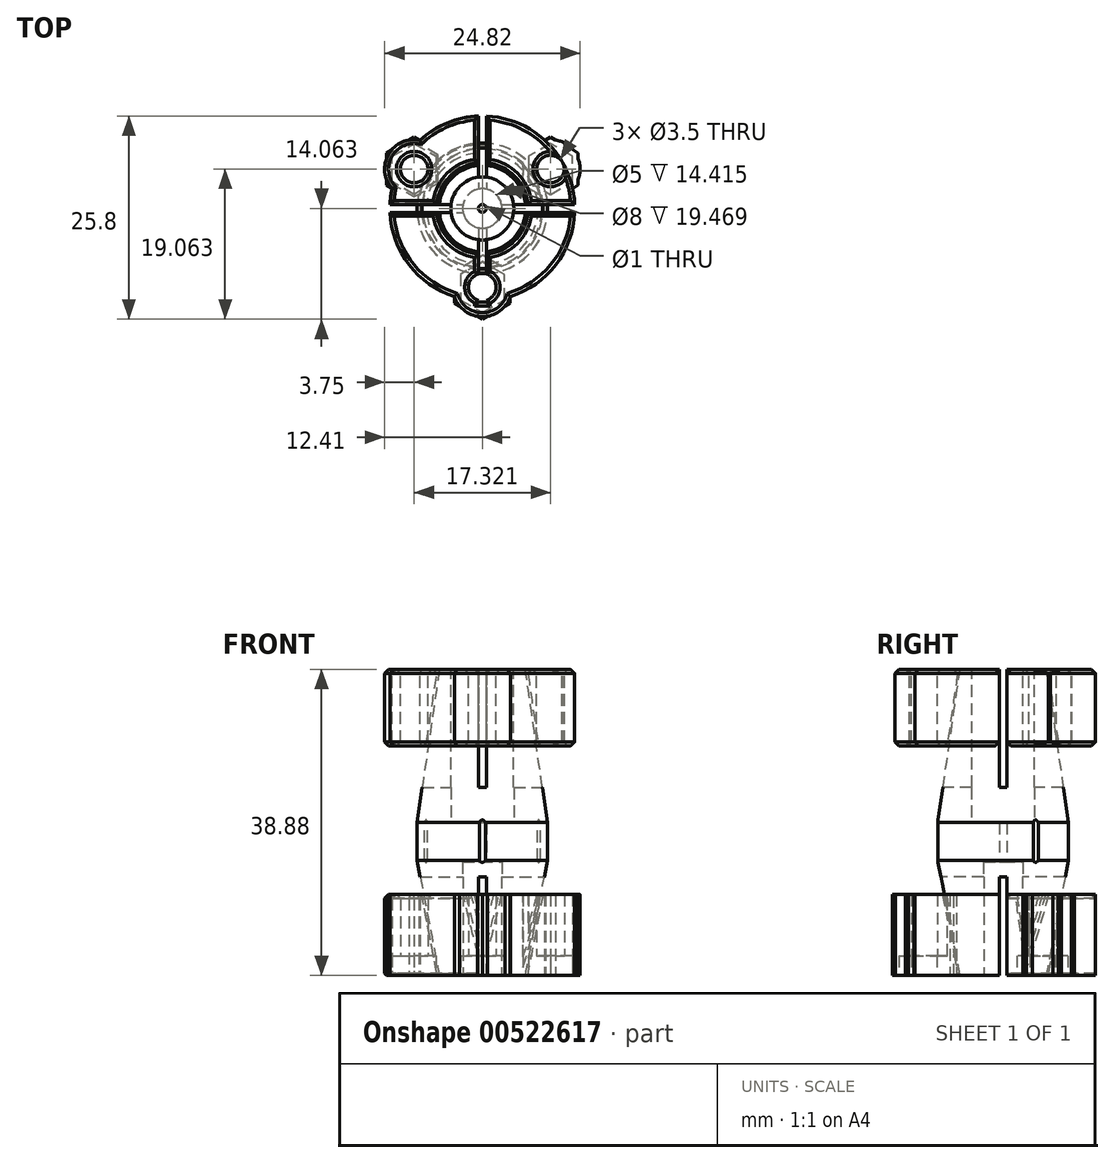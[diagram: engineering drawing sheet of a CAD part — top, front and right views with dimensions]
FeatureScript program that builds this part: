
annotation { "Feature Type Name" : "Feature", "Feature Type Description" : "" }
export const myFeature = defineFeature(function(context is Context, id is Id, definition is map)
    precondition{}
    {
        {
            var Q0;
            Q0=qCreatedBy(makeId("Right.planeOp"),FACE);
            var sketch = newSketch(context, id + "F0", { "sketchPlane" : qUnion([Q0])});
            skLineSegment(sketch, "E0", {"start": v(7.15, -27.2) * mm, "end": v(7.15, -12.78) * mm});
            skLineSegment(sketch, "E1", {"start": v(7.15, -12.78) * mm, "end": v(5.15, -12.78) * mm});
            skLineSegment(sketch, "E2", {"start": v(5.15, -12.78) * mm, "end": v(5.15, -7.78) * mm});
            skLineSegment(sketch, "E3", {"start": v(5.15, -7.78) * mm, "end": v(8.65, -7.78) * mm});
            skLineSegment(sketch, "E4", {"start": v(8.65, -7.78) * mm, "end": v(8.65, 11.68) * mm});
            skLineSegment(sketch, "E5", {"start": v(8.65, 11.68) * mm, "end": v(10.13, 11.68) * mm});
            skLineSegment(sketch, "E6", {"start": v(10.13, 11.68) * mm, "end": v(12.95, -7.78) * mm});
            skLineSegment(sketch, "E7", {"start": v(12.95, -7.78) * mm, "end": v(12.95, -12.57) * mm});
            skLineSegment(sketch, "E8", {"start": v(12.95, -12.57) * mm, "end": v(10.13, -27.2) * mm});
            skLineSegment(sketch, "E9", {"start": v(10.13, -27.2) * mm, "end": v(7.15, -27.2) * mm});
            skLineSegment(sketch, "E10", {"start": v(4.65, -27.22) * mm, "end": v(4.65, -0.97) * mm});
            skLineSegment(sketch, "E11", {"start": v(11.8, 1.95) * mm, "end": v(10.39, 11.68) * mm});
            skPoint(sketch, "E11.startSnap0", {"position": v(11.54, 1.95) * mm});
            skLineSegment(sketch, "E12", {"start": v(10.39, 11.68) * mm, "end": v(16.4, 11.68) * mm});
            skLineSegment(sketch, "E13", {"start": v(16.4, 11.68) * mm, "end": v(16.4, 1.95) * mm});
            skLineSegment(sketch, "E14", {"start": v(16.4, 1.95) * mm, "end": v(11.8, 1.95) * mm});
            skLineSegment(sketch, "E15", {"start": v(10.39, -27.2) * mm, "end": v(12.37, -16.92) * mm});
            skLineSegment(sketch, "E16", {"start": v(12.37, -16.92) * mm, "end": v(16.4, -16.92) * mm});
            skLineSegment(sketch, "E17", {"start": v(16.4, -16.92) * mm, "end": v(16.4, -27.2) * mm});
            skLineSegment(sketch, "E18", {"start": v(16.4, -27.2) * mm, "end": v(10.39, -27.2) * mm});
            skSolve(sketch);
        }
        {
            var Q0;
            Q0=makeQuery(id+"F0.imprint","IMPRINT",FACE,{"disambiguationData":[TD([[makeQuery(id+"F0.imprint","IMPRINT",EDGE,{"derivedFrom":sQuery(id+"F0.wireOp",EDGE,"E0")}),-1.0]])]});
            var Q1;
            Q1=sQuery(id+"F0.wireOp",EDGE,"E10");
            revolve(context, id + "F1", {"entities" : qUnion([Q0]), "axis" : qUnion([Q1]), "revolveType" : RevolveType.FULL});
        }
        {
            var Q0;
            Q0=makeQuery(id+"F0.imprint","IMPRINT",FACE,{"disambiguationData":[TD([[makeQuery(id+"F0.imprint","IMPRINT",EDGE,{"derivedFrom":sQuery(id+"F0.wireOp",EDGE,"E11")}),-1.0]])]});
            var Q1;
            Q1=makeQuery(id+"F0.imprint","IMPRINT",FACE,{"disambiguationData":[TD([[makeQuery(id+"F0.imprint","IMPRINT",EDGE,{"derivedFrom":sQuery(id+"F0.wireOp",EDGE,"E15")}),-1.0]])]});
            var Q2;
            Q2=sQuery(id+"F0.wireOp",EDGE,"E10");
            revolve(context, id + "F2", {"entities" : qUnion([Q0, Q1]), "axis" : qUnion([Q2]), "revolveType" : RevolveType.FULL});
        }
        {
            var Q0;
            Q0=makeQuery(id+"F2.opRevolve","SWEPT_FACE",FACE,{"disambiguationData":[OSD([sQuery(id+"F0.wireOp",EDGE,"E12")])]});
            var sketch = newSketch(context, id + "F3", { "sketchPlane" : qUnion([Q0])});
            skCircle(sketch, "E19", {"center": v(0, 4.65) * mm, "radius": 10 * mm});
            skCircle(sketch, "E20", {"center": v(0, -5.35) * mm, "radius": 1.75 * mm});
            skCircle(sketch, "E21", {"center": v(0, -5.35) * mm, "radius": 3.75 * mm});
            skCircle(sketch, "E22.1.0", {"center": v(8.66, 9.65) * mm, "radius": 1.75 * mm});
            skCircle(sketch, "E22.1.1", {"center": v(8.66, 9.65) * mm, "radius": 3.75 * mm});
            skCircle(sketch, "E22.2.0", {"center": v(-8.66, 9.65) * mm, "radius": 1.75 * mm});
            skCircle(sketch, "E22.2.1", {"center": v(-8.66, 9.65) * mm, "radius": 3.75 * mm});
            skSolve(sketch);
        }
        {
            var Q0;
            {var subQ0=sQuery(id+"F3.wireOp",EDGE,"E20");var subQ1=makeQuery(id+"F2.opRevolve","SWEPT_EDGE",EDGE,{"disambiguationData":[OSD([sQuery(id+"F0.wireOp",EDGE,"E12"),sQuery(id+"F0.wireOp",EDGE,"E13")])]});var subQ2=makeQuery(id+"F3.imprint","INTERSECT",VERTEX,{"disambiguationData":[OD(0.0)],"derivedFrom":[subQ1,subQ0]});Q0=makeQuery(id+"F3.imprint","IMPRINT",FACE,{"disambiguationData":[TD([[makeQuery(id+"F3.imprint","IMPRINT",EDGE,{"disambiguationData":[TD([[subQ2,-1.0]])],"derivedFrom":subQ0}),-1.0]])]});}
            var Q1;
            {var subQ0=sQuery(id+"F3.wireOp",EDGE,"E22.2.0");var subQ1=makeQuery(id+"F2.opRevolve","SWEPT_EDGE",EDGE,{"disambiguationData":[OSD([sQuery(id+"F0.wireOp",EDGE,"E12"),sQuery(id+"F0.wireOp",EDGE,"E13")])]});var subQ2=makeQuery(id+"F3.imprint","INTERSECT",VERTEX,{"disambiguationData":[OD(0.0)],"derivedFrom":[subQ1,subQ0]});Q1=makeQuery(id+"F3.imprint","IMPRINT",FACE,{"disambiguationData":[TD([[makeQuery(id+"F3.imprint","IMPRINT",EDGE,{"disambiguationData":[TD([[subQ2,-1.0]])],"derivedFrom":subQ0}),-1.0]])]});}
            var Q2;
            {var subQ0=sQuery(id+"F3.wireOp",EDGE,"E22.1.0");var subQ1=makeQuery(id+"F2.opRevolve","SWEPT_EDGE",EDGE,{"disambiguationData":[OSD([sQuery(id+"F0.wireOp",EDGE,"E12"),sQuery(id+"F0.wireOp",EDGE,"E13")])]});var subQ2=makeQuery(id+"F3.imprint","INTERSECT",VERTEX,{"disambiguationData":[OD(0.0)],"derivedFrom":[subQ1,subQ0]});Q2=makeQuery(id+"F3.imprint","IMPRINT",FACE,{"disambiguationData":[TD([[makeQuery(id+"F3.imprint","IMPRINT",EDGE,{"disambiguationData":[TD([[subQ2,-1.0]])],"derivedFrom":subQ0}),-1.0]])]});}
            var Q3;
            Q3=makeQuery(id+"F2.opRevolve","SWEPT_FACE",FACE,{"disambiguationData":[OSD([sQuery(id+"F0.wireOp",EDGE,"E14")])]});
            extrude(context, id + "F4", {"entities" : qUnion([Q0, Q1, Q2]), "operationType" : NewBodyOperationType.ADD, "endBound" : BoundingType.UP_TO_SURFACE, "oppositeDirection" : true, "endBoundEntityFace" : qUnion([Q3]), "depth" : 25 * mm});
        }
        {
            var Q0;
            {var subQ0=sQuery(id+"F3.wireOp",EDGE,"E20");var subQ1=sQuery(id+"F3.wireOp",EDGE,"E19");var subQ2=makeQuery(id+"F3.imprint","INTERSECT",VERTEX,{"disambiguationData":[OD(0.0)],"derivedFrom":[subQ1,subQ0]});Q0=makeQuery(id+"F3.imprint","IMPRINT",FACE,{"disambiguationData":[TD([[makeQuery(id+"F3.imprint","IMPRINT",EDGE,{"disambiguationData":[TD([[subQ2,-1.0]])],"derivedFrom":subQ1}),-1.0]])]});}
            var Q1;
            {var subQ0=sQuery(id+"F3.wireOp",EDGE,"E20");var subQ1=sQuery(id+"F3.wireOp",EDGE,"E19");var subQ2=makeQuery(id+"F3.imprint","INTERSECT",VERTEX,{"disambiguationData":[OD(0.0)],"derivedFrom":[subQ1,subQ0]});Q1=makeQuery(id+"F3.imprint","IMPRINT",FACE,{"disambiguationData":[TD([[makeQuery(id+"F3.imprint","IMPRINT",EDGE,{"disambiguationData":[TD([[subQ2,-1.0]])],"derivedFrom":subQ1}),1.0]])]});}
            var Q2;
            {var subQ0=sQuery(id+"F3.wireOp",EDGE,"E22.1.0");var subQ1=sQuery(id+"F3.wireOp",EDGE,"E19");var subQ2=makeQuery(id+"F3.imprint","INTERSECT",VERTEX,{"disambiguationData":[OD(0.0)],"derivedFrom":[subQ1,subQ0]});Q2=makeQuery(id+"F3.imprint","IMPRINT",FACE,{"disambiguationData":[TD([[makeQuery(id+"F3.imprint","IMPRINT",EDGE,{"disambiguationData":[TD([[subQ2,-1.0]])],"derivedFrom":subQ1}),1.0]])]});}
            var Q3;
            {var subQ0=sQuery(id+"F3.wireOp",EDGE,"E22.1.0");var subQ1=sQuery(id+"F3.wireOp",EDGE,"E19");var subQ2=makeQuery(id+"F3.imprint","INTERSECT",VERTEX,{"disambiguationData":[OD(0.0)],"derivedFrom":[subQ1,subQ0]});Q3=makeQuery(id+"F3.imprint","IMPRINT",FACE,{"disambiguationData":[TD([[makeQuery(id+"F3.imprint","IMPRINT",EDGE,{"disambiguationData":[TD([[subQ2,-1.0]])],"derivedFrom":subQ1}),-1.0]])]});}
            var Q4;
            {var subQ0=sQuery(id+"F3.wireOp",EDGE,"E22.2.0");var subQ1=sQuery(id+"F3.wireOp",EDGE,"E19");var subQ2=makeQuery(id+"F3.imprint","INTERSECT",VERTEX,{"disambiguationData":[OD(0.0)],"derivedFrom":[subQ1,subQ0]});Q4=makeQuery(id+"F3.imprint","IMPRINT",FACE,{"disambiguationData":[TD([[makeQuery(id+"F3.imprint","IMPRINT",EDGE,{"disambiguationData":[TD([[subQ2,-1.0]])],"derivedFrom":subQ1}),1.0]])]});}
            var Q5;
            {var subQ0=sQuery(id+"F3.wireOp",EDGE,"E22.2.0");var subQ1=sQuery(id+"F3.wireOp",EDGE,"E19");var subQ2=makeQuery(id+"F3.imprint","INTERSECT",VERTEX,{"disambiguationData":[OD(0.0)],"derivedFrom":[subQ1,subQ0]});Q5=makeQuery(id+"F3.imprint","IMPRINT",FACE,{"disambiguationData":[TD([[makeQuery(id+"F3.imprint","IMPRINT",EDGE,{"disambiguationData":[TD([[subQ2,-1.0]])],"derivedFrom":subQ1}),-1.0]])]});}
            extrude(context, id + "F5", {"entities" : qUnion([Q0, Q1, Q2, Q3, Q4, Q5]), "operationType" : NewBodyOperationType.REMOVE, "oppositeDirection" : true, "depth" : 25 * mm});
        }
        {
            var Q0;
            Q0=makeQuery(id+"F2.opRevolve","SWEPT_FACE",FACE,{"disambiguationData":[OSD([sQuery(id+"F0.wireOp",EDGE,"E18")])]});
            var sketch = newSketch(context, id + "F6", { "sketchPlane" : qUnion([Q0])});
            skArc(sketch, "E23.0.0", {"start": v(-3.55, 6.54) * mm, "mid": v(-10.17, 1.22) * mm, "end": v(-11.47, -7.17) * mm});
            skArc(sketch, "E23.0.1", {"start": v(-11.47, -7.17) * mm, "mid": v(-11.9, -11.53) * mm, "end": v(-7.92, -13.33) * mm});
            skArc(sketch, "E23.0.2", {"start": v(-7.92, -13.33) * mm, "mid": v(0, -16.4) * mm, "end": v(7.92, -13.33) * mm});
            skArc(sketch, "E23.0.3", {"start": v(7.92, -13.33) * mm, "mid": v(11.9, -11.53) * mm, "end": v(11.47, -7.17) * mm});
            skArc(sketch, "E23.0.4", {"start": v(11.47, -7.17) * mm, "mid": v(10.17, 1.22) * mm, "end": v(3.55, 6.54) * mm});
            skArc(sketch, "E23.0.5", {"start": v(3.55, 6.54) * mm, "mid": v(0, 9.1) * mm, "end": v(-3.55, 6.54) * mm});
            skCircle(sketch, "E24", {"center": v(8.66, -9.65) * mm, "radius": 1.75 * mm});
            skCircle(sketch, "E25", {"center": v(-8.66, -9.65) * mm, "radius": 1.75 * mm});
            skCircle(sketch, "E26", {"center": v(0, 5.35) * mm, "radius": 1.75 * mm});
            skSolve(sketch);
        }
        {
            var Q0;
            {var subQ0=sQuery(id+"F6.wireOp",EDGE,"E23.0.5");Q0=makeQuery(id+"F6.imprint","IMPRINT",FACE,{"disambiguationData":[TD([[makeQuery(id+"F6.imprint","IMPRINT",EDGE,{"derivedFrom":subQ0}),1.0]])]});}
            var Q1;
            {var subQ0=sQuery(id+"F6.wireOp",EDGE,"E23.0.3");Q1=makeQuery(id+"F6.imprint","IMPRINT",FACE,{"disambiguationData":[TD([[makeQuery(id+"F6.imprint","IMPRINT",EDGE,{"derivedFrom":subQ0}),1.0]])]});}
            var Q2;
            {var subQ0=sQuery(id+"F6.wireOp",EDGE,"E23.0.1");Q2=makeQuery(id+"F6.imprint","IMPRINT",FACE,{"disambiguationData":[TD([[makeQuery(id+"F6.imprint","IMPRINT",EDGE,{"derivedFrom":subQ0}),1.0]])]});}
            var Q3;
            Q3=makeQuery(id+"F2.opRevolve","SWEPT_FACE",FACE,{"disambiguationData":[OSD([sQuery(id+"F0.wireOp",EDGE,"E16")])]});
            extrude(context, id + "F7", {"entities" : qUnion([Q0, Q1, Q2]), "operationType" : NewBodyOperationType.ADD, "endBound" : BoundingType.UP_TO_SURFACE, "oppositeDirection" : true, "endBoundEntityFace" : qUnion([Q3]), "depth" : 25 * mm});
        }
        {
            var Q0;
            {var subQ0=sQuery(id+"F6.wireOp",EDGE,"E26");var subQ1=makeQuery(id+"F2.opRevolve","SWEPT_EDGE",EDGE,{"disambiguationData":[OSD([sQuery(id+"F0.wireOp",EDGE,"E17"),sQuery(id+"F0.wireOp",EDGE,"E18")])]});var subQ2=makeQuery(id+"F6.imprint","INTERSECT",VERTEX,{"disambiguationData":[OD(0.0)],"derivedFrom":[subQ1,subQ0]});Q0=makeQuery(id+"F6.imprint","IMPRINT",FACE,{"disambiguationData":[TD([[makeQuery(id+"F6.imprint","IMPRINT",EDGE,{"disambiguationData":[TD([[subQ2,-1.0]])],"derivedFrom":subQ0}),1.0]])]});}
            var Q1;
            {var subQ0=sQuery(id+"F6.wireOp",EDGE,"E25");var subQ1=makeQuery(id+"F2.opRevolve","SWEPT_EDGE",EDGE,{"disambiguationData":[OSD([sQuery(id+"F0.wireOp",EDGE,"E17"),sQuery(id+"F0.wireOp",EDGE,"E18")])]});var subQ2=makeQuery(id+"F6.imprint","INTERSECT",VERTEX,{"disambiguationData":[OD(0.0)],"derivedFrom":[subQ1,subQ0]});Q1=makeQuery(id+"F6.imprint","IMPRINT",FACE,{"disambiguationData":[TD([[makeQuery(id+"F6.imprint","IMPRINT",EDGE,{"disambiguationData":[TD([[subQ2,1.0]])],"derivedFrom":subQ0}),1.0]])]});}
            var Q2;
            {var subQ0=sQuery(id+"F6.wireOp",EDGE,"E24");var subQ1=makeQuery(id+"F2.opRevolve","SWEPT_EDGE",EDGE,{"disambiguationData":[OSD([sQuery(id+"F0.wireOp",EDGE,"E17"),sQuery(id+"F0.wireOp",EDGE,"E18")])]});var subQ2=makeQuery(id+"F6.imprint","INTERSECT",VERTEX,{"disambiguationData":[OD(0.0)],"derivedFrom":[subQ1,subQ0]});Q2=makeQuery(id+"F6.imprint","IMPRINT",FACE,{"disambiguationData":[TD([[makeQuery(id+"F6.imprint","IMPRINT",EDGE,{"disambiguationData":[TD([[subQ2,1.0]])],"derivedFrom":subQ0}),1.0]])]});}
            extrude(context, id + "F8", {"entities" : qUnion([Q0, Q1, Q2]), "operationType" : NewBodyOperationType.REMOVE, "oppositeDirection" : true, "depth" : 25 * mm});
        }
        {
            var Q0;
            Q0=makeQuery(id+"F1.opRevolve","SWEPT_FACE",FACE,{"disambiguationData":[OSD([sQuery(id+"F0.wireOp",EDGE,"E5")])]});
            var sketch = newSketch(context, id + "F9", { "sketchPlane" : qUnion([Q0])});
            skLineSegment(sketch, "E27.bottom", {"start": v(0.5, 16.55) * mm, "end": v(-0.5, 16.55) * mm});
            skLineSegment(sketch, "E27.top", {"start": v(0.5, -7.24) * mm, "end": v(-0.5, -7.24) * mm});
            skLineSegment(sketch, "E27.left", {"start": v(0.5, 16.55) * mm, "end": v(0.5, -7.24) * mm});
            skLineSegment(sketch, "E27.right", {"start": v(-0.5, 16.55) * mm, "end": v(-0.5, -7.24) * mm});
            skLineSegment(sketch, "E28.bottom", {"start": v(-15.2, 5.15) * mm, "end": v(15.2, 5.15) * mm});
            skLineSegment(sketch, "E28.top", {"start": v(-15.2, 4.15) * mm, "end": v(15.2, 4.15) * mm});
            skLineSegment(sketch, "E28.left", {"start": v(-15.2, 5.15) * mm, "end": v(-15.2, 4.15) * mm});
            skLineSegment(sketch, "E28.right", {"start": v(15.2, 5.15) * mm, "end": v(15.2, 4.15) * mm});
            skPoint(sketch, "E28.middle", {"position": v(0, 4.65) * mm});
            skSolve(sketch);
        }
        {
            var Q0;
            {var subQ0=sQuery(id+"F9.wireOp",EDGE,"E28.bottom");var subQ1=sQuery(id+"F9.wireOp",EDGE,"E27.left");var subQ2=makeQuery(id+"F9.imprint","INTERSECT",VERTEX,{"derivedFrom":[subQ1,subQ0]});Q0=makeQuery(id+"F9.imprint","IMPRINT",FACE,{"disambiguationData":[TD([[makeQuery(id+"F9.imprint","IMPRINT",EDGE,{"disambiguationData":[TD([[subQ2,-1.0]])],"derivedFrom":subQ1}),-1.0]])]});}
            var Q1;
            {var subQ0=sQuery(id+"F9.wireOp",EDGE,"E27.bottom");Q1=makeQuery(id+"F9.imprint","IMPRINT",FACE,{"disambiguationData":[TD([[makeQuery(id+"F9.imprint","IMPRINT",EDGE,{"derivedFrom":subQ0}),1.0]])]});}
            var Q2;
            {var subQ0=sQuery(id+"F9.wireOp",EDGE,"E27.top");Q2=makeQuery(id+"F9.imprint","IMPRINT",FACE,{"disambiguationData":[TD([[makeQuery(id+"F9.imprint","IMPRINT",EDGE,{"derivedFrom":subQ0}),-1.0]])]});}
            var Q3;
            {var subQ0=sQuery(id+"F9.wireOp",EDGE,"E28.bottom");var subQ1=sQuery(id+"F9.wireOp",EDGE,"E27.left");var subQ2=makeQuery(id+"F9.imprint","INTERSECT",VERTEX,{"derivedFrom":[subQ1,subQ0]});Q3=makeQuery(id+"F9.imprint","IMPRINT",FACE,{"disambiguationData":[TD([[makeQuery(id+"F9.imprint","IMPRINT",EDGE,{"disambiguationData":[TD([[subQ2,1.0]])],"derivedFrom":subQ0}),1.0]])]});}
            var Q4;
            {var subQ0=sQuery(id+"F9.wireOp",EDGE,"E28.top");var subQ1=sQuery(id+"F9.wireOp",EDGE,"E27.left");var subQ2=makeQuery(id+"F9.imprint","INTERSECT",VERTEX,{"derivedFrom":[subQ1,subQ0]});Q4=makeQuery(id+"F9.imprint","IMPRINT",FACE,{"disambiguationData":[TD([[makeQuery(id+"F9.imprint","IMPRINT",EDGE,{"disambiguationData":[TD([[subQ2,1.0]])],"derivedFrom":subQ0}),-1.0]])]});}
            var Q5;
            {var subQ0=sQuery(id+"F9.wireOp",EDGE,"E27.left");var subQ1=sQuery(id+"F0.wireOp",EDGE,"E5");var subQ2=makeQuery(id+"F1.opRevolve","SWEPT_EDGE",EDGE,{"disambiguationData":[OSD([subQ1,sQuery(id+"F0.wireOp",EDGE,"E6")])]});var subQ3=makeQuery(id+"F9.imprint","INTERSECT",VERTEX,{"disambiguationData":[OD(0.0)],"derivedFrom":[subQ2,subQ0]});Q5=makeQuery(id+"F9.imprint","IMPRINT",FACE,{"disambiguationData":[TD([[makeQuery(id+"F9.imprint","IMPRINT",EDGE,{"disambiguationData":[TD([[subQ3,-1.0]])],"derivedFrom":subQ0}),-1.0]])]});}
            var Q6;
            {var subQ0=sQuery(id+"F9.wireOp",EDGE,"E28.bottom");var subQ1=sQuery(id+"F9.wireOp",EDGE,"E27.left");var subQ2=makeQuery(id+"F9.imprint","INTERSECT",VERTEX,{"derivedFrom":[subQ1,subQ0]});Q6=makeQuery(id+"F9.imprint","IMPRINT",FACE,{"disambiguationData":[TD([[makeQuery(id+"F9.imprint","IMPRINT",EDGE,{"disambiguationData":[TD([[subQ2,-1.0]])],"derivedFrom":subQ1}),-1.0]])]});}
            var Q7;
            {var subQ0=sQuery(id+"F9.wireOp",EDGE,"E27.bottom");Q7=makeQuery(id+"F9.imprint","IMPRINT",FACE,{"disambiguationData":[TD([[makeQuery(id+"F9.imprint","IMPRINT",EDGE,{"derivedFrom":subQ0}),1.0]])]});}
            var Q8;
            {var subQ0=sQuery(id+"F9.wireOp",EDGE,"E27.top");Q8=makeQuery(id+"F9.imprint","IMPRINT",FACE,{"disambiguationData":[TD([[makeQuery(id+"F9.imprint","IMPRINT",EDGE,{"derivedFrom":subQ0}),-1.0]])]});}
            var Q9;
            {var subQ0=sQuery(id+"F9.wireOp",EDGE,"E28.bottom");var subQ1=sQuery(id+"F9.wireOp",EDGE,"E27.left");var subQ2=makeQuery(id+"F9.imprint","INTERSECT",VERTEX,{"derivedFrom":[subQ1,subQ0]});Q9=makeQuery(id+"F9.imprint","IMPRINT",FACE,{"disambiguationData":[TD([[makeQuery(id+"F9.imprint","IMPRINT",EDGE,{"disambiguationData":[TD([[subQ2,1.0]])],"derivedFrom":subQ0}),1.0]])]});}
            var Q10;
            {var subQ0=sQuery(id+"F9.wireOp",EDGE,"E28.top");var subQ1=sQuery(id+"F9.wireOp",EDGE,"E27.left");var subQ2=makeQuery(id+"F9.imprint","INTERSECT",VERTEX,{"derivedFrom":[subQ1,subQ0]});Q10=makeQuery(id+"F9.imprint","IMPRINT",FACE,{"disambiguationData":[TD([[makeQuery(id+"F9.imprint","IMPRINT",EDGE,{"disambiguationData":[TD([[subQ2,1.0]])],"derivedFrom":subQ0}),-1.0]])]});}
            var Q11;
            {var subQ0=sQuery(id+"F9.wireOp",EDGE,"E27.left");var subQ1=sQuery(id+"F0.wireOp",EDGE,"E5");var subQ2=makeQuery(id+"F1.opRevolve","SWEPT_EDGE",EDGE,{"disambiguationData":[OSD([subQ1,sQuery(id+"F0.wireOp",EDGE,"E6")])]});var subQ3=makeQuery(id+"F9.imprint","INTERSECT",VERTEX,{"disambiguationData":[OD(0.0)],"derivedFrom":[subQ2,subQ0]});Q11=makeQuery(id+"F9.imprint","IMPRINT",FACE,{"disambiguationData":[TD([[makeQuery(id+"F9.imprint","IMPRINT",EDGE,{"disambiguationData":[TD([[subQ3,-1.0]])],"derivedFrom":subQ0}),-1.0]])]});}
            var Q12;
            {var subQ0=sQuery(id+"F9.wireOp",EDGE,"E28.bottom");var subQ1=sQuery(id+"F9.wireOp",EDGE,"E27.left");var subQ2=makeQuery(id+"F9.imprint","INTERSECT",VERTEX,{"derivedFrom":[subQ1,subQ0]});Q12=makeQuery(id+"F9.imprint","IMPRINT",FACE,{"disambiguationData":[TD([[makeQuery(id+"F9.imprint","IMPRINT",EDGE,{"disambiguationData":[TD([[subQ2,-1.0]])],"derivedFrom":subQ1}),-1.0]])]});}
            var Q13;
            {var subQ0=sQuery(id+"F9.wireOp",EDGE,"E27.bottom");Q13=makeQuery(id+"F9.imprint","IMPRINT",FACE,{"disambiguationData":[TD([[makeQuery(id+"F9.imprint","IMPRINT",EDGE,{"derivedFrom":subQ0}),1.0]])]});}
            var Q14;
            {var subQ0=sQuery(id+"F9.wireOp",EDGE,"E27.top");Q14=makeQuery(id+"F9.imprint","IMPRINT",FACE,{"disambiguationData":[TD([[makeQuery(id+"F9.imprint","IMPRINT",EDGE,{"derivedFrom":subQ0}),-1.0]])]});}
            var Q15;
            {var subQ0=sQuery(id+"F9.wireOp",EDGE,"E28.bottom");var subQ1=sQuery(id+"F9.wireOp",EDGE,"E27.left");var subQ2=makeQuery(id+"F9.imprint","INTERSECT",VERTEX,{"derivedFrom":[subQ1,subQ0]});Q15=makeQuery(id+"F9.imprint","IMPRINT",FACE,{"disambiguationData":[TD([[makeQuery(id+"F9.imprint","IMPRINT",EDGE,{"disambiguationData":[TD([[subQ2,1.0]])],"derivedFrom":subQ0}),1.0]])]});}
            var Q16;
            {var subQ0=sQuery(id+"F9.wireOp",EDGE,"E28.top");var subQ1=sQuery(id+"F9.wireOp",EDGE,"E27.left");var subQ2=makeQuery(id+"F9.imprint","INTERSECT",VERTEX,{"derivedFrom":[subQ1,subQ0]});Q16=makeQuery(id+"F9.imprint","IMPRINT",FACE,{"disambiguationData":[TD([[makeQuery(id+"F9.imprint","IMPRINT",EDGE,{"disambiguationData":[TD([[subQ2,1.0]])],"derivedFrom":subQ0}),-1.0]])]});}
            var Q17;
            {var subQ0=sQuery(id+"F9.wireOp",EDGE,"E27.left");var subQ1=sQuery(id+"F0.wireOp",EDGE,"E5");var subQ2=makeQuery(id+"F1.opRevolve","SWEPT_EDGE",EDGE,{"disambiguationData":[OSD([subQ1,sQuery(id+"F0.wireOp",EDGE,"E6")])]});var subQ3=makeQuery(id+"F9.imprint","INTERSECT",VERTEX,{"disambiguationData":[OD(0.0)],"derivedFrom":[subQ2,subQ0]});Q17=makeQuery(id+"F9.imprint","IMPRINT",FACE,{"disambiguationData":[TD([[makeQuery(id+"F9.imprint","IMPRINT",EDGE,{"disambiguationData":[TD([[subQ3,-1.0]])],"derivedFrom":subQ0}),-1.0]])]});}
            var Q18;
            {var subQ0=sQuery(id+"F9.wireOp",EDGE,"E28.bottom");var subQ1=sQuery(id+"F9.wireOp",EDGE,"E27.left");var subQ2=makeQuery(id+"F9.imprint","INTERSECT",VERTEX,{"derivedFrom":[subQ1,subQ0]});Q18=makeQuery(id+"F9.imprint","IMPRINT",FACE,{"disambiguationData":[TD([[makeQuery(id+"F9.imprint","IMPRINT",EDGE,{"disambiguationData":[TD([[subQ2,-1.0]])],"derivedFrom":subQ1}),-1.0]])]});}
            var Q19;
            {var subQ0=sQuery(id+"F9.wireOp",EDGE,"E27.bottom");Q19=makeQuery(id+"F9.imprint","IMPRINT",FACE,{"disambiguationData":[TD([[makeQuery(id+"F9.imprint","IMPRINT",EDGE,{"derivedFrom":subQ0}),1.0]])]});}
            var Q20;
            {var subQ0=sQuery(id+"F9.wireOp",EDGE,"E27.top");Q20=makeQuery(id+"F9.imprint","IMPRINT",FACE,{"disambiguationData":[TD([[makeQuery(id+"F9.imprint","IMPRINT",EDGE,{"derivedFrom":subQ0}),-1.0]])]});}
            var Q21;
            {var subQ0=sQuery(id+"F9.wireOp",EDGE,"E28.bottom");var subQ1=sQuery(id+"F9.wireOp",EDGE,"E27.left");var subQ2=makeQuery(id+"F9.imprint","INTERSECT",VERTEX,{"derivedFrom":[subQ1,subQ0]});Q21=makeQuery(id+"F9.imprint","IMPRINT",FACE,{"disambiguationData":[TD([[makeQuery(id+"F9.imprint","IMPRINT",EDGE,{"disambiguationData":[TD([[subQ2,1.0]])],"derivedFrom":subQ0}),1.0]])]});}
            var Q22;
            {var subQ0=sQuery(id+"F9.wireOp",EDGE,"E28.top");var subQ1=sQuery(id+"F9.wireOp",EDGE,"E27.left");var subQ2=makeQuery(id+"F9.imprint","INTERSECT",VERTEX,{"derivedFrom":[subQ1,subQ0]});Q22=makeQuery(id+"F9.imprint","IMPRINT",FACE,{"disambiguationData":[TD([[makeQuery(id+"F9.imprint","IMPRINT",EDGE,{"disambiguationData":[TD([[subQ2,1.0]])],"derivedFrom":subQ0}),-1.0]])]});}
            var Q23;
            {var subQ0=sQuery(id+"F9.wireOp",EDGE,"E27.left");var subQ1=sQuery(id+"F0.wireOp",EDGE,"E5");var subQ2=makeQuery(id+"F1.opRevolve","SWEPT_EDGE",EDGE,{"disambiguationData":[OSD([subQ1,sQuery(id+"F0.wireOp",EDGE,"E6")])]});var subQ3=makeQuery(id+"F9.imprint","INTERSECT",VERTEX,{"disambiguationData":[OD(0.0)],"derivedFrom":[subQ2,subQ0]});Q23=makeQuery(id+"F9.imprint","IMPRINT",FACE,{"disambiguationData":[TD([[makeQuery(id+"F9.imprint","IMPRINT",EDGE,{"disambiguationData":[TD([[subQ3,-1.0]])],"derivedFrom":subQ0}),-1.0]])]});}
            var Q24;
            {var subQ0=sQuery(id+"F9.wireOp",EDGE,"E27.top");Q24=makeQuery(id+"F9.imprint","IMPRINT",FACE,{"disambiguationData":[TD([[makeQuery(id+"F9.imprint","IMPRINT",EDGE,{"derivedFrom":subQ0}),-1.0]])]});}
            var Q25;
            {var subQ0=sQuery(id+"F9.wireOp",EDGE,"E28.top");var subQ1=sQuery(id+"F9.wireOp",EDGE,"E27.left");var subQ2=makeQuery(id+"F9.imprint","INTERSECT",VERTEX,{"derivedFrom":[subQ1,subQ0]});Q25=makeQuery(id+"F9.imprint","IMPRINT",FACE,{"disambiguationData":[TD([[makeQuery(id+"F9.imprint","IMPRINT",EDGE,{"disambiguationData":[TD([[subQ2,-1.0]])],"derivedFrom":subQ1}),1.0]])]});}
            var Q26;
            {var subQ0=sQuery(id+"F9.wireOp",EDGE,"E28.top");var subQ1=sQuery(id+"F9.wireOp",EDGE,"E27.right");var subQ2=makeQuery(id+"F9.imprint","INTERSECT",VERTEX,{"derivedFrom":[subQ1,subQ0]});Q26=makeQuery(id+"F9.imprint","IMPRINT",FACE,{"disambiguationData":[TD([[makeQuery(id+"F9.imprint","IMPRINT",EDGE,{"disambiguationData":[TD([[subQ2,-1.0]])],"derivedFrom":subQ1}),-1.0]])]});}
            var Q27;
            {var subQ0=sQuery(id+"F9.wireOp",EDGE,"E28.top");var subQ1=sQuery(id+"F9.wireOp",EDGE,"E27.left");var subQ2=makeQuery(id+"F9.imprint","INTERSECT",VERTEX,{"derivedFrom":[subQ1,subQ0]});Q27=makeQuery(id+"F9.imprint","IMPRINT",FACE,{"disambiguationData":[TD([[makeQuery(id+"F9.imprint","IMPRINT",EDGE,{"disambiguationData":[TD([[subQ2,-1.0]])],"derivedFrom":subQ1}),1.0]])]});}
            var Q28;
            {var subQ0=sQuery(id+"F9.wireOp",EDGE,"E28.top");var subQ1=sQuery(id+"F9.wireOp",EDGE,"E27.right");var subQ2=makeQuery(id+"F9.imprint","INTERSECT",VERTEX,{"derivedFrom":[subQ1,subQ0]});Q28=makeQuery(id+"F9.imprint","IMPRINT",FACE,{"disambiguationData":[TD([[makeQuery(id+"F9.imprint","IMPRINT",EDGE,{"disambiguationData":[TD([[subQ2,-1.0]])],"derivedFrom":subQ1}),-1.0]])]});}
            var Q29;
            {var subQ0=sQuery(id+"F9.wireOp",EDGE,"E28.bottom");var subQ1=sQuery(id+"F9.wireOp",EDGE,"E27.left");var subQ2=makeQuery(id+"F9.imprint","INTERSECT",VERTEX,{"derivedFrom":[subQ1,subQ0]});Q29=makeQuery(id+"F9.imprint","IMPRINT",FACE,{"disambiguationData":[TD([[makeQuery(id+"F9.imprint","IMPRINT",EDGE,{"disambiguationData":[TD([[subQ2,-1.0]])],"derivedFrom":subQ1}),-1.0]])]});}
            var Q30;
            {var subQ0=sQuery(id+"F9.wireOp",EDGE,"E27.bottom");Q30=makeQuery(id+"F9.imprint","IMPRINT",FACE,{"disambiguationData":[TD([[makeQuery(id+"F9.imprint","IMPRINT",EDGE,{"derivedFrom":subQ0}),1.0]])]});}
            var Q31;
            {var subQ0=sQuery(id+"F9.wireOp",EDGE,"E27.top");Q31=makeQuery(id+"F9.imprint","IMPRINT",FACE,{"disambiguationData":[TD([[makeQuery(id+"F9.imprint","IMPRINT",EDGE,{"derivedFrom":subQ0}),-1.0]])]});}
            var Q32;
            {var subQ0=sQuery(id+"F9.wireOp",EDGE,"E28.bottom");var subQ1=sQuery(id+"F9.wireOp",EDGE,"E27.left");var subQ2=makeQuery(id+"F9.imprint","INTERSECT",VERTEX,{"derivedFrom":[subQ1,subQ0]});Q32=makeQuery(id+"F9.imprint","IMPRINT",FACE,{"disambiguationData":[TD([[makeQuery(id+"F9.imprint","IMPRINT",EDGE,{"disambiguationData":[TD([[subQ2,1.0]])],"derivedFrom":subQ0}),1.0]])]});}
            var Q33;
            {var subQ0=sQuery(id+"F9.wireOp",EDGE,"E28.top");var subQ1=sQuery(id+"F9.wireOp",EDGE,"E27.left");var subQ2=makeQuery(id+"F9.imprint","INTERSECT",VERTEX,{"derivedFrom":[subQ1,subQ0]});Q33=makeQuery(id+"F9.imprint","IMPRINT",FACE,{"disambiguationData":[TD([[makeQuery(id+"F9.imprint","IMPRINT",EDGE,{"disambiguationData":[TD([[subQ2,1.0]])],"derivedFrom":subQ0}),-1.0]])]});}
            var Q34;
            {var subQ0=sQuery(id+"F9.wireOp",EDGE,"E27.left");var subQ1=sQuery(id+"F0.wireOp",EDGE,"E5");var subQ2=makeQuery(id+"F1.opRevolve","SWEPT_EDGE",EDGE,{"disambiguationData":[OSD([subQ1,sQuery(id+"F0.wireOp",EDGE,"E6")])]});var subQ3=makeQuery(id+"F9.imprint","INTERSECT",VERTEX,{"disambiguationData":[OD(0.0)],"derivedFrom":[subQ2,subQ0]});Q34=makeQuery(id+"F9.imprint","IMPRINT",FACE,{"disambiguationData":[TD([[makeQuery(id+"F9.imprint","IMPRINT",EDGE,{"disambiguationData":[TD([[subQ3,-1.0]])],"derivedFrom":subQ0}),-1.0]])]});}
            var Q35;
            {var subQ0=sQuery(id+"F9.wireOp",EDGE,"E27.left");var subQ1=sQuery(id+"F0.wireOp",EDGE,"E5");var subQ2=makeQuery(id+"F1.opRevolve","SWEPT_EDGE",EDGE,{"disambiguationData":[OSD([subQ1,sQuery(id+"F0.wireOp",EDGE,"E6")])]});var subQ3=makeQuery(id+"F9.imprint","INTERSECT",VERTEX,{"disambiguationData":[OD(1.0)],"derivedFrom":[subQ2,subQ0]});Q35=makeQuery(id+"F9.imprint","IMPRINT",FACE,{"disambiguationData":[TD([[makeQuery(id+"F9.imprint","IMPRINT",EDGE,{"disambiguationData":[TD([[subQ3,1.0]])],"derivedFrom":subQ0}),-1.0]])]});}
            var Q36;
            {var subQ0=sQuery(id+"F9.wireOp",EDGE,"E28.bottom");var subQ1=sQuery(id+"F9.wireOp",EDGE,"E27.left");var subQ2=makeQuery(id+"F9.imprint","INTERSECT",VERTEX,{"derivedFrom":[subQ1,subQ0]});Q36=makeQuery(id+"F9.imprint","IMPRINT",FACE,{"disambiguationData":[TD([[makeQuery(id+"F9.imprint","IMPRINT",EDGE,{"disambiguationData":[TD([[subQ2,-1.0]])],"derivedFrom":subQ1}),-1.0]])]});}
            var Q37;
            {var subQ0=sQuery(id+"F9.wireOp",EDGE,"E27.bottom");Q37=makeQuery(id+"F9.imprint","IMPRINT",FACE,{"disambiguationData":[TD([[makeQuery(id+"F9.imprint","IMPRINT",EDGE,{"derivedFrom":subQ0}),1.0]])]});}
            var Q38;
            {var subQ0=sQuery(id+"F9.wireOp",EDGE,"E27.top");Q38=makeQuery(id+"F9.imprint","IMPRINT",FACE,{"disambiguationData":[TD([[makeQuery(id+"F9.imprint","IMPRINT",EDGE,{"derivedFrom":subQ0}),-1.0]])]});}
            var Q39;
            {var subQ0=sQuery(id+"F9.wireOp",EDGE,"E28.bottom");var subQ1=sQuery(id+"F9.wireOp",EDGE,"E27.left");var subQ2=makeQuery(id+"F9.imprint","INTERSECT",VERTEX,{"derivedFrom":[subQ1,subQ0]});Q39=makeQuery(id+"F9.imprint","IMPRINT",FACE,{"disambiguationData":[TD([[makeQuery(id+"F9.imprint","IMPRINT",EDGE,{"disambiguationData":[TD([[subQ2,1.0]])],"derivedFrom":subQ0}),1.0]])]});}
            var Q40;
            {var subQ0=sQuery(id+"F9.wireOp",EDGE,"E28.top");var subQ1=sQuery(id+"F9.wireOp",EDGE,"E27.left");var subQ2=makeQuery(id+"F9.imprint","INTERSECT",VERTEX,{"derivedFrom":[subQ1,subQ0]});Q40=makeQuery(id+"F9.imprint","IMPRINT",FACE,{"disambiguationData":[TD([[makeQuery(id+"F9.imprint","IMPRINT",EDGE,{"disambiguationData":[TD([[subQ2,1.0]])],"derivedFrom":subQ0}),-1.0]])]});}
            var Q41;
            {var subQ0=sQuery(id+"F9.wireOp",EDGE,"E27.left");var subQ1=sQuery(id+"F0.wireOp",EDGE,"E5");var subQ2=makeQuery(id+"F1.opRevolve","SWEPT_EDGE",EDGE,{"disambiguationData":[OSD([subQ1,sQuery(id+"F0.wireOp",EDGE,"E6")])]});var subQ3=makeQuery(id+"F9.imprint","INTERSECT",VERTEX,{"disambiguationData":[OD(0.0)],"derivedFrom":[subQ2,subQ0]});Q41=makeQuery(id+"F9.imprint","IMPRINT",FACE,{"disambiguationData":[TD([[makeQuery(id+"F9.imprint","IMPRINT",EDGE,{"disambiguationData":[TD([[subQ3,-1.0]])],"derivedFrom":subQ0}),-1.0]])]});}
            var Q42;
            {var subQ0=sQuery(id+"F9.wireOp",EDGE,"E27.left");var subQ1=sQuery(id+"F0.wireOp",EDGE,"E5");var subQ2=makeQuery(id+"F1.opRevolve","SWEPT_EDGE",EDGE,{"disambiguationData":[OSD([subQ1,sQuery(id+"F0.wireOp",EDGE,"E6")])]});var subQ3=makeQuery(id+"F9.imprint","INTERSECT",VERTEX,{"disambiguationData":[OD(1.0)],"derivedFrom":[subQ2,subQ0]});Q42=makeQuery(id+"F9.imprint","IMPRINT",FACE,{"disambiguationData":[TD([[makeQuery(id+"F9.imprint","IMPRINT",EDGE,{"disambiguationData":[TD([[subQ3,1.0]])],"derivedFrom":subQ0}),-1.0]])]});}
            var Q43;
            {var subQ0=sQuery(id+"F9.wireOp",EDGE,"E28.bottom");var subQ1=sQuery(id+"F9.wireOp",EDGE,"E27.left");var subQ2=makeQuery(id+"F9.imprint","INTERSECT",VERTEX,{"derivedFrom":[subQ1,subQ0]});Q43=makeQuery(id+"F9.imprint","IMPRINT",FACE,{"disambiguationData":[TD([[makeQuery(id+"F9.imprint","IMPRINT",EDGE,{"disambiguationData":[TD([[subQ2,-1.0]])],"derivedFrom":subQ1}),-1.0]])]});}
            var Q44;
            {var subQ0=sQuery(id+"F9.wireOp",EDGE,"E27.bottom");Q44=makeQuery(id+"F9.imprint","IMPRINT",FACE,{"disambiguationData":[TD([[makeQuery(id+"F9.imprint","IMPRINT",EDGE,{"derivedFrom":subQ0}),1.0]])]});}
            var Q45;
            {var subQ0=sQuery(id+"F9.wireOp",EDGE,"E27.top");Q45=makeQuery(id+"F9.imprint","IMPRINT",FACE,{"disambiguationData":[TD([[makeQuery(id+"F9.imprint","IMPRINT",EDGE,{"derivedFrom":subQ0}),-1.0]])]});}
            var Q46;
            {var subQ0=sQuery(id+"F9.wireOp",EDGE,"E28.bottom");var subQ1=sQuery(id+"F9.wireOp",EDGE,"E27.left");var subQ2=makeQuery(id+"F9.imprint","INTERSECT",VERTEX,{"derivedFrom":[subQ1,subQ0]});Q46=makeQuery(id+"F9.imprint","IMPRINT",FACE,{"disambiguationData":[TD([[makeQuery(id+"F9.imprint","IMPRINT",EDGE,{"disambiguationData":[TD([[subQ2,1.0]])],"derivedFrom":subQ0}),1.0]])]});}
            var Q47;
            {var subQ0=sQuery(id+"F9.wireOp",EDGE,"E28.top");var subQ1=sQuery(id+"F9.wireOp",EDGE,"E27.left");var subQ2=makeQuery(id+"F9.imprint","INTERSECT",VERTEX,{"derivedFrom":[subQ1,subQ0]});Q47=makeQuery(id+"F9.imprint","IMPRINT",FACE,{"disambiguationData":[TD([[makeQuery(id+"F9.imprint","IMPRINT",EDGE,{"disambiguationData":[TD([[subQ2,1.0]])],"derivedFrom":subQ0}),-1.0]])]});}
            var Q48;
            {var subQ0=sQuery(id+"F9.wireOp",EDGE,"E27.left");var subQ1=sQuery(id+"F0.wireOp",EDGE,"E5");var subQ2=makeQuery(id+"F1.opRevolve","SWEPT_EDGE",EDGE,{"disambiguationData":[OSD([subQ1,sQuery(id+"F0.wireOp",EDGE,"E6")])]});var subQ3=makeQuery(id+"F9.imprint","INTERSECT",VERTEX,{"disambiguationData":[OD(0.0)],"derivedFrom":[subQ2,subQ0]});Q48=makeQuery(id+"F9.imprint","IMPRINT",FACE,{"disambiguationData":[TD([[makeQuery(id+"F9.imprint","IMPRINT",EDGE,{"disambiguationData":[TD([[subQ3,-1.0]])],"derivedFrom":subQ0}),-1.0]])]});}
            var Q49;
            {var subQ0=sQuery(id+"F9.wireOp",EDGE,"E27.left");var subQ1=sQuery(id+"F0.wireOp",EDGE,"E5");var subQ2=makeQuery(id+"F1.opRevolve","SWEPT_EDGE",EDGE,{"disambiguationData":[OSD([subQ1,sQuery(id+"F0.wireOp",EDGE,"E6")])]});var subQ3=makeQuery(id+"F9.imprint","INTERSECT",VERTEX,{"disambiguationData":[OD(1.0)],"derivedFrom":[subQ2,subQ0]});Q49=makeQuery(id+"F9.imprint","IMPRINT",FACE,{"disambiguationData":[TD([[makeQuery(id+"F9.imprint","IMPRINT",EDGE,{"disambiguationData":[TD([[subQ3,1.0]])],"derivedFrom":subQ0}),-1.0]])]});}
            var Q50;
            {var subQ0=sQuery(id+"F9.wireOp",EDGE,"E28.bottom");var subQ1=sQuery(id+"F9.wireOp",EDGE,"E27.left");var subQ2=makeQuery(id+"F9.imprint","INTERSECT",VERTEX,{"derivedFrom":[subQ1,subQ0]});Q50=makeQuery(id+"F9.imprint","IMPRINT",FACE,{"disambiguationData":[TD([[makeQuery(id+"F9.imprint","IMPRINT",EDGE,{"disambiguationData":[TD([[subQ2,1.0]])],"derivedFrom":subQ1}),1.0]])]});}
            var Q51;
            {var subQ0=sQuery(id+"F9.wireOp",EDGE,"E28.bottom");var subQ1=sQuery(id+"F9.wireOp",EDGE,"E27.right");var subQ2=makeQuery(id+"F9.imprint","INTERSECT",VERTEX,{"derivedFrom":[subQ1,subQ0]});Q51=makeQuery(id+"F9.imprint","IMPRINT",FACE,{"disambiguationData":[TD([[makeQuery(id+"F9.imprint","IMPRINT",EDGE,{"disambiguationData":[TD([[subQ2,1.0]])],"derivedFrom":subQ1}),-1.0]])]});}
            var Q52;
            {var subQ0=sQuery(id+"F9.wireOp",EDGE,"E28.bottom");var subQ1=sQuery(id+"F9.wireOp",EDGE,"E27.left");var subQ2=makeQuery(id+"F9.imprint","INTERSECT",VERTEX,{"derivedFrom":[subQ1,subQ0]});Q52=makeQuery(id+"F9.imprint","IMPRINT",FACE,{"disambiguationData":[TD([[makeQuery(id+"F9.imprint","IMPRINT",EDGE,{"disambiguationData":[TD([[subQ2,1.0]])],"derivedFrom":subQ1}),1.0]])]});}
            var Q53;
            {var subQ0=sQuery(id+"F9.wireOp",EDGE,"E28.bottom");var subQ1=sQuery(id+"F9.wireOp",EDGE,"E27.right");var subQ2=makeQuery(id+"F9.imprint","INTERSECT",VERTEX,{"derivedFrom":[subQ1,subQ0]});Q53=makeQuery(id+"F9.imprint","IMPRINT",FACE,{"disambiguationData":[TD([[makeQuery(id+"F9.imprint","IMPRINT",EDGE,{"disambiguationData":[TD([[subQ2,1.0]])],"derivedFrom":subQ1}),-1.0]])]});}
            var Q54;
            {var subQ0=sQuery(id+"F9.wireOp",EDGE,"E27.bottom");Q54=makeQuery(id+"F9.imprint","IMPRINT",FACE,{"disambiguationData":[TD([[makeQuery(id+"F9.imprint","IMPRINT",EDGE,{"derivedFrom":subQ0}),1.0]])]});}
            var Q55;
            {var subQ0=sQuery(id+"F9.wireOp",EDGE,"E28.bottom");var subQ1=sQuery(id+"F9.wireOp",EDGE,"E27.left");var subQ2=makeQuery(id+"F9.imprint","INTERSECT",VERTEX,{"derivedFrom":[subQ1,subQ0]});Q55=makeQuery(id+"F9.imprint","IMPRINT",FACE,{"disambiguationData":[TD([[makeQuery(id+"F9.imprint","IMPRINT",EDGE,{"disambiguationData":[TD([[subQ2,1.0]])],"derivedFrom":subQ1}),1.0]])]});}
            var Q56;
            {var subQ0=sQuery(id+"F9.wireOp",EDGE,"E28.top");var subQ1=sQuery(id+"F9.wireOp",EDGE,"E27.left");var subQ2=makeQuery(id+"F9.imprint","INTERSECT",VERTEX,{"derivedFrom":[subQ1,subQ0]});Q56=makeQuery(id+"F9.imprint","IMPRINT",FACE,{"disambiguationData":[TD([[makeQuery(id+"F9.imprint","IMPRINT",EDGE,{"disambiguationData":[TD([[subQ2,-1.0]])],"derivedFrom":subQ1}),1.0]])]});}
            var Q57;
            {var subQ0=sQuery(id+"F9.wireOp",EDGE,"E28.bottom");var subQ1=sQuery(id+"F9.wireOp",EDGE,"E27.left");var subQ2=makeQuery(id+"F9.imprint","INTERSECT",VERTEX,{"derivedFrom":[subQ1,subQ0]});Q57=makeQuery(id+"F9.imprint","IMPRINT",FACE,{"disambiguationData":[TD([[makeQuery(id+"F9.imprint","IMPRINT",EDGE,{"disambiguationData":[TD([[subQ2,1.0]])],"derivedFrom":subQ1}),1.0]])]});}
            var Q58;
            {var subQ0=sQuery(id+"F9.wireOp",EDGE,"E28.top");var subQ1=sQuery(id+"F9.wireOp",EDGE,"E27.left");var subQ2=makeQuery(id+"F9.imprint","INTERSECT",VERTEX,{"derivedFrom":[subQ1,subQ0]});Q58=makeQuery(id+"F9.imprint","IMPRINT",FACE,{"disambiguationData":[TD([[makeQuery(id+"F9.imprint","IMPRINT",EDGE,{"disambiguationData":[TD([[subQ2,-1.0]])],"derivedFrom":subQ1}),1.0]])]});}
            var Q59;
            {var subQ0=sQuery(id+"F9.wireOp",EDGE,"E28.right");Q59=makeQuery(id+"F9.imprint","IMPRINT",FACE,{"disambiguationData":[TD([[makeQuery(id+"F9.imprint","IMPRINT",EDGE,{"derivedFrom":subQ0}),-1.0]])]});}
            var Q60;
            {var subQ0=sQuery(id+"F9.wireOp",EDGE,"E28.bottom");var subQ1=sQuery(id+"F9.wireOp",EDGE,"E27.right");var subQ2=makeQuery(id+"F9.imprint","INTERSECT",VERTEX,{"derivedFrom":[subQ1,subQ0]});Q60=makeQuery(id+"F9.imprint","IMPRINT",FACE,{"disambiguationData":[TD([[makeQuery(id+"F9.imprint","IMPRINT",EDGE,{"disambiguationData":[TD([[subQ2,1.0]])],"derivedFrom":subQ1}),-1.0]])]});}
            var Q61;
            {var subQ0=sQuery(id+"F9.wireOp",EDGE,"E28.top");var subQ1=sQuery(id+"F9.wireOp",EDGE,"E27.right");var subQ2=makeQuery(id+"F9.imprint","INTERSECT",VERTEX,{"derivedFrom":[subQ1,subQ0]});Q61=makeQuery(id+"F9.imprint","IMPRINT",FACE,{"disambiguationData":[TD([[makeQuery(id+"F9.imprint","IMPRINT",EDGE,{"disambiguationData":[TD([[subQ2,-1.0]])],"derivedFrom":subQ1}),-1.0]])]});}
            var Q62;
            {var subQ0=sQuery(id+"F9.wireOp",EDGE,"E28.bottom");var subQ1=sQuery(id+"F9.wireOp",EDGE,"E27.right");var subQ2=makeQuery(id+"F9.imprint","INTERSECT",VERTEX,{"derivedFrom":[subQ1,subQ0]});Q62=makeQuery(id+"F9.imprint","IMPRINT",FACE,{"disambiguationData":[TD([[makeQuery(id+"F9.imprint","IMPRINT",EDGE,{"disambiguationData":[TD([[subQ2,1.0]])],"derivedFrom":subQ1}),-1.0]])]});}
            var Q63;
            {var subQ0=sQuery(id+"F9.wireOp",EDGE,"E28.top");var subQ1=sQuery(id+"F9.wireOp",EDGE,"E27.right");var subQ2=makeQuery(id+"F9.imprint","INTERSECT",VERTEX,{"derivedFrom":[subQ1,subQ0]});Q63=makeQuery(id+"F9.imprint","IMPRINT",FACE,{"disambiguationData":[TD([[makeQuery(id+"F9.imprint","IMPRINT",EDGE,{"disambiguationData":[TD([[subQ2,-1.0]])],"derivedFrom":subQ1}),-1.0]])]});}
            var Q64;
            {var subQ0=sQuery(id+"F9.wireOp",EDGE,"E28.left");Q64=makeQuery(id+"F9.imprint","IMPRINT",FACE,{"disambiguationData":[TD([[makeQuery(id+"F9.imprint","IMPRINT",EDGE,{"derivedFrom":subQ0}),1.0]])]});}
            var Q65;
            {var subQ0=sQuery(id+"F9.wireOp",EDGE,"E28.bottom");var subQ1=sQuery(id+"F0.wireOp",EDGE,"E5");var subQ2=makeQuery(id+"F1.opRevolve","SWEPT_EDGE",EDGE,{"disambiguationData":[OSD([subQ1,sQuery(id+"F0.wireOp",EDGE,"E6")])]});var subQ3=makeQuery(id+"F9.imprint","INTERSECT",VERTEX,{"disambiguationData":[OD(0.0)],"derivedFrom":[subQ2,subQ0]});Q65=makeQuery(id+"F9.imprint","IMPRINT",FACE,{"disambiguationData":[TD([[makeQuery(id+"F9.imprint","IMPRINT",EDGE,{"disambiguationData":[TD([[subQ3,-1.0]])],"derivedFrom":subQ0}),-1.0]])]});}
            var Q66;
            {var subQ0=sQuery(id+"F9.wireOp",EDGE,"E28.bottom");var subQ1=sQuery(id+"F0.wireOp",EDGE,"E5");var subQ2=makeQuery(id+"F1.opRevolve","SWEPT_EDGE",EDGE,{"disambiguationData":[OSD([subQ1,sQuery(id+"F0.wireOp",EDGE,"E6")])]});var subQ3=makeQuery(id+"F9.imprint","INTERSECT",VERTEX,{"disambiguationData":[OD(1.0)],"derivedFrom":[subQ2,subQ0]});Q66=makeQuery(id+"F9.imprint","IMPRINT",FACE,{"disambiguationData":[TD([[makeQuery(id+"F9.imprint","IMPRINT",EDGE,{"disambiguationData":[TD([[subQ3,1.0]])],"derivedFrom":subQ0}),-1.0]])]});}
            extrude(context, id + "F10", {"entities" : qUnion([Q0, Q1, Q2, Q3, Q4, Q5, Q6, Q7, Q8, Q9, Q10, Q11, Q12, Q13, Q14, Q15, Q16, Q17, Q18, Q19, Q20, Q21, Q22, Q23, Q24, Q25, Q26, Q27, Q28, Q29, Q30, Q31, Q32, Q33, Q34, Q35, Q36, Q37, Q38, Q39, Q40, Q41, Q42, Q43, Q44, Q45, Q46, Q47, Q48, Q49, Q50, Q51, Q52, Q53, Q54, Q55, Q56, Q57, Q58, Q59, Q60, Q61, Q62, Q63, Q64, Q65, Q66]), "operationType" : NewBodyOperationType.REMOVE, "oppositeDirection" : true, "depth" : 15 * mm});
        }
        {
            var Q0;
            {var subQ0=sQuery(id+"F9.wireOp",EDGE,"E28.bottom");var subQ1=sQuery(id+"F9.wireOp",EDGE,"E27.left");var subQ2=makeQuery(id+"F9.imprint","INTERSECT",VERTEX,{"derivedFrom":[subQ1,subQ0]});Q0=makeQuery(id+"F9.imprint","IMPRINT",FACE,{"disambiguationData":[TD([[makeQuery(id+"F9.imprint","IMPRINT",EDGE,{"disambiguationData":[TD([[subQ2,-1.0]])],"derivedFrom":subQ1}),1.0]])]});}
            var Q1;
            {var subQ0=sQuery(id+"F9.wireOp",EDGE,"E28.bottom");var subQ1=sQuery(id+"F0.wireOp",EDGE,"E5");var subQ2=makeQuery(id+"F1.opRevolve","SWEPT_EDGE",EDGE,{"disambiguationData":[OSD([subQ1,sQuery(id+"F0.wireOp",EDGE,"E6")])]});var subQ3=makeQuery(id+"F9.imprint","INTERSECT",VERTEX,{"disambiguationData":[OD(1.0)],"derivedFrom":[subQ2,subQ0]});Q1=makeQuery(id+"F9.imprint","IMPRINT",FACE,{"disambiguationData":[TD([[makeQuery(id+"F9.imprint","IMPRINT",EDGE,{"disambiguationData":[TD([[subQ3,1.0]])],"derivedFrom":subQ0}),-1.0]])]});}
            var Q2;
            {var subQ0=sQuery(id+"F9.wireOp",EDGE,"E28.right");Q2=makeQuery(id+"F9.imprint","IMPRINT",FACE,{"disambiguationData":[TD([[makeQuery(id+"F9.imprint","IMPRINT",EDGE,{"derivedFrom":subQ0}),-1.0]])]});}
            var Q3;
            {var subQ0=sQuery(id+"F9.wireOp",EDGE,"E28.bottom");var subQ1=sQuery(id+"F9.wireOp",EDGE,"E27.left");var subQ2=makeQuery(id+"F9.imprint","INTERSECT",VERTEX,{"derivedFrom":[subQ1,subQ0]});Q3=makeQuery(id+"F9.imprint","IMPRINT",FACE,{"disambiguationData":[TD([[makeQuery(id+"F9.imprint","IMPRINT",EDGE,{"disambiguationData":[TD([[subQ2,1.0]])],"derivedFrom":subQ0}),1.0]])]});}
            var Q4;
            {var subQ0=sQuery(id+"F9.wireOp",EDGE,"E27.left");var subQ1=sQuery(id+"F0.wireOp",EDGE,"E5");var subQ2=makeQuery(id+"F1.opRevolve","SWEPT_EDGE",EDGE,{"disambiguationData":[OSD([subQ1,sQuery(id+"F0.wireOp",EDGE,"E6")])]});var subQ3=makeQuery(id+"F9.imprint","INTERSECT",VERTEX,{"disambiguationData":[OD(0.0)],"derivedFrom":[subQ2,subQ0]});Q4=makeQuery(id+"F9.imprint","IMPRINT",FACE,{"disambiguationData":[TD([[makeQuery(id+"F9.imprint","IMPRINT",EDGE,{"disambiguationData":[TD([[subQ3,-1.0]])],"derivedFrom":subQ0}),-1.0]])]});}
            var Q5;
            {var subQ0=sQuery(id+"F9.wireOp",EDGE,"E27.bottom");Q5=makeQuery(id+"F9.imprint","IMPRINT",FACE,{"disambiguationData":[TD([[makeQuery(id+"F9.imprint","IMPRINT",EDGE,{"derivedFrom":subQ0}),1.0]])]});}
            var Q6;
            {var subQ0=sQuery(id+"F9.wireOp",EDGE,"E27.top");Q6=makeQuery(id+"F9.imprint","IMPRINT",FACE,{"disambiguationData":[TD([[makeQuery(id+"F9.imprint","IMPRINT",EDGE,{"derivedFrom":subQ0}),-1.0]])]});}
            var Q7;
            {var subQ0=sQuery(id+"F9.wireOp",EDGE,"E27.left");var subQ1=sQuery(id+"F0.wireOp",EDGE,"E5");var subQ2=makeQuery(id+"F1.opRevolve","SWEPT_EDGE",EDGE,{"disambiguationData":[OSD([subQ1,sQuery(id+"F0.wireOp",EDGE,"E6")])]});var subQ3=makeQuery(id+"F9.imprint","INTERSECT",VERTEX,{"disambiguationData":[OD(1.0)],"derivedFrom":[subQ2,subQ0]});Q7=makeQuery(id+"F9.imprint","IMPRINT",FACE,{"disambiguationData":[TD([[makeQuery(id+"F9.imprint","IMPRINT",EDGE,{"disambiguationData":[TD([[subQ3,1.0]])],"derivedFrom":subQ0}),-1.0]])]});}
            var Q8;
            {var subQ0=sQuery(id+"F9.wireOp",EDGE,"E28.top");var subQ1=sQuery(id+"F9.wireOp",EDGE,"E27.left");var subQ2=makeQuery(id+"F9.imprint","INTERSECT",VERTEX,{"derivedFrom":[subQ1,subQ0]});Q8=makeQuery(id+"F9.imprint","IMPRINT",FACE,{"disambiguationData":[TD([[makeQuery(id+"F9.imprint","IMPRINT",EDGE,{"disambiguationData":[TD([[subQ2,1.0]])],"derivedFrom":subQ0}),-1.0]])]});}
            var Q9;
            {var subQ0=sQuery(id+"F9.wireOp",EDGE,"E28.left");Q9=makeQuery(id+"F9.imprint","IMPRINT",FACE,{"disambiguationData":[TD([[makeQuery(id+"F9.imprint","IMPRINT",EDGE,{"derivedFrom":subQ0}),1.0]])]});}
            var Q10;
            {var subQ0=sQuery(id+"F9.wireOp",EDGE,"E28.bottom");var subQ1=sQuery(id+"F0.wireOp",EDGE,"E5");var subQ2=makeQuery(id+"F1.opRevolve","SWEPT_EDGE",EDGE,{"disambiguationData":[OSD([subQ1,sQuery(id+"F0.wireOp",EDGE,"E6")])]});var subQ3=makeQuery(id+"F9.imprint","INTERSECT",VERTEX,{"disambiguationData":[OD(0.0)],"derivedFrom":[subQ2,subQ0]});Q10=makeQuery(id+"F9.imprint","IMPRINT",FACE,{"disambiguationData":[TD([[makeQuery(id+"F9.imprint","IMPRINT",EDGE,{"disambiguationData":[TD([[subQ3,-1.0]])],"derivedFrom":subQ0}),-1.0]])]});}
            var Q11;
            {var subQ0=sQuery(id+"F9.wireOp",EDGE,"E28.bottom");var subQ1=sQuery(id+"F9.wireOp",EDGE,"E27.right");var subQ2=makeQuery(id+"F9.imprint","INTERSECT",VERTEX,{"derivedFrom":[subQ1,subQ0]});Q11=makeQuery(id+"F9.imprint","IMPRINT",FACE,{"disambiguationData":[TD([[makeQuery(id+"F9.imprint","IMPRINT",EDGE,{"disambiguationData":[TD([[subQ2,-1.0]])],"derivedFrom":subQ1}),-1.0]])]});}
            extrude(context, id + "F11", {"entities" : qUnion([Q0, Q1, Q2, Q3, Q4, Q5, Q6, Q7, Q8, Q9, Q10, Q11]), "operationType" : NewBodyOperationType.REMOVE, "oppositeDirection" : true, "depth" : 44.88 * mm, "hasSecondDirection" : true, "secondDirectionOppositeDirection" : true, "secondDirectionDepth" : 26.34 * mm});
        }
        {
            var Q0;
            {var subQ0=sQuery(id+"F0.wireOp",EDGE,"E18");var subQ1=sQuery(id+"F0.wireOp",EDGE,"E17");Q0=makeQuery(id+"F7.boolean.opBoolean","MERGE",FACE,{"derivedFrom":[makeQuery(id+"F2.opRevolve","SWEPT_FACE",FACE,{"disambiguationData":[OSD([subQ0])]}),makeQuery(id+"F7.opExtrude","CAP_FACE",FACE,{"disambiguationData":[OSD([subQ1,subQ0,sQuery(id+"F6.wireOp",EDGE,"E23.0.1"),sQuery(id+"F6.wireOp",EDGE,"E25")])],"isStart":true}),makeQuery(id+"F7.opExtrude","CAP_FACE",FACE,{"disambiguationData":[OSD([subQ1,subQ0,sQuery(id+"F6.wireOp",EDGE,"E23.0.3"),sQuery(id+"F6.wireOp",EDGE,"E24")])],"isStart":true}),makeQuery(id+"F7.opExtrude","CAP_FACE",FACE,{"disambiguationData":[OSD([subQ1,subQ0,sQuery(id+"F6.wireOp",EDGE,"E23.0.5"),sQuery(id+"F6.wireOp",EDGE,"E26")])],"isStart":true})]});}
            var sketch = newSketch(context, id + "F12", { "sketchPlane" : qUnion([Q0])});
            skCircle(sketch, "E29.cCircle", {"center": v(8.66, -9.65) * mm, "radius": 2.8 * mm, "construction": true});
            skLineSegment(sketch, "E29.0", {"start": v(5.86, -11.27) * mm, "end": v(5.86, -8.04) * mm});
            skLineSegment(sketch, "E29.1", {"start": v(5.86, -8.04) * mm, "end": v(8.66, -6.42) * mm});
            skLineSegment(sketch, "E29.2", {"start": v(8.66, -6.42) * mm, "end": v(11.46, -8.04) * mm});
            skLineSegment(sketch, "E29.3", {"start": v(11.46, -8.04) * mm, "end": v(11.46, -11.27) * mm});
            skLineSegment(sketch, "E29.4", {"start": v(11.46, -11.27) * mm, "end": v(8.66, -12.89) * mm});
            skLineSegment(sketch, "E29.5", {"start": v(8.66, -12.89) * mm, "end": v(5.86, -11.27) * mm});
            skPoint(sketch, "E29.0.midPoint", {"position": v(5.86, -9.65) * mm});
            skCircle(sketch, "E30.cCircle", {"center": v(8.66, -9.65) * mm, "radius": 3.52 * mm, "construction": true});
            skLineSegment(sketch, "E30.0", {"start": v(5.14, -11.68) * mm, "end": v(5.14, -7.62) * mm});
            skLineSegment(sketch, "E30.1", {"start": v(5.14, -7.62) * mm, "end": v(8.66, -5.6) * mm});
            skLineSegment(sketch, "E30.2", {"start": v(8.66, -5.6) * mm, "end": v(12.18, -7.62) * mm});
            skLineSegment(sketch, "E30.3", {"start": v(12.18, -7.62) * mm, "end": v(12.18, -11.68) * mm});
            skLineSegment(sketch, "E30.4", {"start": v(12.18, -11.68) * mm, "end": v(8.66, -13.71) * mm});
            skLineSegment(sketch, "E30.5", {"start": v(8.66, -13.71) * mm, "end": v(5.14, -11.68) * mm});
            skPoint(sketch, "E30.0.midPoint", {"position": v(5.14, -9.65) * mm});
            skLineSegment(sketch, "E31.1.0", {"start": v(0, 9.4) * mm, "end": v(3.52, 7.38) * mm});
            skLineSegment(sketch, "E31.1.1", {"start": v(3.52, 7.38) * mm, "end": v(3.52, 3.32) * mm});
            skLineSegment(sketch, "E31.1.2", {"start": v(2.8, 6.96) * mm, "end": v(2.8, 3.73) * mm});
            skLineSegment(sketch, "E31.1.3", {"start": v(0, 8.58) * mm, "end": v(2.8, 6.96) * mm});
            skLineSegment(sketch, "E31.1.4", {"start": v(-3.52, 7.38) * mm, "end": v(0, 9.4) * mm});
            skLineSegment(sketch, "E31.1.5", {"start": v(-3.52, 3.32) * mm, "end": v(-3.52, 7.38) * mm});
            skLineSegment(sketch, "E31.1.6", {"start": v(0, 1.29) * mm, "end": v(-3.52, 3.32) * mm});
            skLineSegment(sketch, "E31.1.7", {"start": v(3.52, 3.32) * mm, "end": v(0, 1.29) * mm});
            skLineSegment(sketch, "E31.1.8", {"start": v(2.8, 3.73) * mm, "end": v(0, 2.11) * mm});
            skLineSegment(sketch, "E31.1.9", {"start": v(0, 2.11) * mm, "end": v(-2.8, 3.73) * mm});
            skLineSegment(sketch, "E31.1.10", {"start": v(-2.8, 3.73) * mm, "end": v(-2.8, 6.96) * mm});
            skLineSegment(sketch, "E31.1.11", {"start": v(-2.8, 6.96) * mm, "end": v(0, 8.58) * mm});
            skLineSegment(sketch, "E31.2.0", {"start": v(-12.18, -11.68) * mm, "end": v(-12.18, -7.62) * mm});
            skLineSegment(sketch, "E31.2.1", {"start": v(-12.18, -7.62) * mm, "end": v(-8.66, -5.6) * mm});
            skLineSegment(sketch, "E31.2.2", {"start": v(-11.46, -8.04) * mm, "end": v(-8.66, -6.42) * mm});
            skLineSegment(sketch, "E31.2.3", {"start": v(-11.46, -11.27) * mm, "end": v(-11.46, -8.04) * mm});
            skLineSegment(sketch, "E31.2.4", {"start": v(-8.66, -13.71) * mm, "end": v(-12.18, -11.68) * mm});
            skLineSegment(sketch, "E31.2.5", {"start": v(-5.14, -11.68) * mm, "end": v(-8.66, -13.71) * mm});
            skLineSegment(sketch, "E31.2.6", {"start": v(-5.14, -7.62) * mm, "end": v(-5.14, -11.68) * mm});
            skLineSegment(sketch, "E31.2.7", {"start": v(-8.66, -5.6) * mm, "end": v(-5.14, -7.62) * mm});
            skLineSegment(sketch, "E31.2.8", {"start": v(-8.66, -6.42) * mm, "end": v(-5.86, -8.04) * mm});
            skLineSegment(sketch, "E31.2.9", {"start": v(-5.86, -8.04) * mm, "end": v(-5.86, -11.27) * mm});
            skLineSegment(sketch, "E31.2.10", {"start": v(-5.86, -11.27) * mm, "end": v(-8.66, -12.89) * mm});
            skLineSegment(sketch, "E31.2.11", {"start": v(-8.66, -12.89) * mm, "end": v(-11.46, -11.27) * mm});
            skPoint(sketch, "E31.center", {"position": v(0, -4.65) * mm});
            skSolve(sketch);
        }
        {
            var Q0;
            {var subQ0=sQuery(id+"F12.wireOp",EDGE,"E30.3");var subQ1=sQuery(id+"F12.wireOp",EDGE,"E30.2");var subQ2=makeQuery(id+"F12.imprint","INTERSECT",VERTEX,{"derivedFrom":[subQ1,subQ0]});Q0=makeQuery(id+"F12.imprint","IMPRINT",FACE,{"disambiguationData":[TD([[makeQuery(id+"F12.imprint","IMPRINT",EDGE,{"disambiguationData":[TD([[subQ2,1.0]])],"derivedFrom":subQ1}),-1.0]])]});}
            var Q1;
            {var subQ0=sQuery(id+"F12.wireOp",EDGE,"E30.4");var subQ1=sQuery(id+"F12.wireOp",EDGE,"E30.3");var subQ2=makeQuery(id+"F12.imprint","INTERSECT",VERTEX,{"derivedFrom":[subQ1,subQ0]});Q1=makeQuery(id+"F12.imprint","IMPRINT",FACE,{"disambiguationData":[TD([[makeQuery(id+"F12.imprint","IMPRINT",EDGE,{"disambiguationData":[TD([[subQ2,1.0]])],"derivedFrom":subQ1}),-1.0]])]});}
            var Q2;
            {var subQ0=sQuery(id+"F12.wireOp",EDGE,"E30.5");var subQ1=sQuery(id+"F12.wireOp",EDGE,"E30.4");var subQ2=makeQuery(id+"F12.imprint","INTERSECT",VERTEX,{"derivedFrom":[subQ1,subQ0]});Q2=makeQuery(id+"F12.imprint","IMPRINT",FACE,{"disambiguationData":[TD([[makeQuery(id+"F12.imprint","IMPRINT",EDGE,{"disambiguationData":[TD([[subQ2,1.0]])],"derivedFrom":subQ1}),-1.0]])]});}
            var Q3;
            {var subQ0=sQuery(id+"F0.wireOp",EDGE,"E18");var subQ1=sQuery(id+"F0.wireOp",EDGE,"E17");Q3=makeQuery(id+"F7.boolean.opBoolean","MERGE",FACE,{"derivedFrom":[makeQuery(id+"F2.opRevolve","SWEPT_FACE",FACE,{"disambiguationData":[OSD([sQuery(id+"F0.wireOp",EDGE,"E16")])]}),makeQuery(id+"F7.opExtrude","CAP_FACE",FACE,{"disambiguationData":[OSD([subQ1,subQ0,sQuery(id+"F6.wireOp",EDGE,"E23.0.1"),sQuery(id+"F6.wireOp",EDGE,"E25")])],"isStart":false}),makeQuery(id+"F7.opExtrude","CAP_FACE",FACE,{"disambiguationData":[OSD([subQ1,subQ0,sQuery(id+"F6.wireOp",EDGE,"E23.0.3"),sQuery(id+"F6.wireOp",EDGE,"E24")])],"isStart":false}),makeQuery(id+"F7.opExtrude","CAP_FACE",FACE,{"disambiguationData":[OSD([subQ1,subQ0,sQuery(id+"F6.wireOp",EDGE,"E23.0.5"),sQuery(id+"F6.wireOp",EDGE,"E26")])],"isStart":false})]});}
            extrude(context, id + "F13", {"entities" : qUnion([Q0, Q1, Q2]), "operationType" : NewBodyOperationType.ADD, "endBound" : BoundingType.UP_TO_SURFACE, "oppositeDirection" : true, "endBoundEntityFace" : qUnion([Q3]), "depth" : 25 * mm});
        }
        {
            var Q0;
            Q0=makeQuery(id+"F12.imprint","IMPRINT",FACE,{"disambiguationData":[TD([[makeQuery(id+"F12.imprint","IMPRINT",EDGE,{"derivedFrom":sQuery(id+"F12.wireOp",EDGE,"E29.0")}),-1.0]])]});
            extrude(context, id + "F14", {"entities" : qUnion([Q0]), "operationType" : NewBodyOperationType.REMOVE, "oppositeDirection" : true, "depth" : 2.5 * mm});
        }
        {
            var Q0;
            {var subQ0=sQuery(id+"F12.wireOp",EDGE,"E31.2.5");var subQ1=sQuery(id+"F12.wireOp",EDGE,"E31.2.4");var subQ2=makeQuery(id+"F12.imprint","INTERSECT",VERTEX,{"derivedFrom":[subQ1,subQ0]});Q0=makeQuery(id+"F12.imprint","IMPRINT",FACE,{"disambiguationData":[TD([[makeQuery(id+"F12.imprint","IMPRINT",EDGE,{"disambiguationData":[TD([[subQ2,-1.0]])],"derivedFrom":subQ1}),-1.0]])]});}
            var Q1;
            {var subQ0=sQuery(id+"F12.wireOp",EDGE,"E31.2.4");var subQ1=sQuery(id+"F12.wireOp",EDGE,"E31.2.0");var subQ2=makeQuery(id+"F12.imprint","INTERSECT",VERTEX,{"derivedFrom":[subQ1,subQ0]});Q1=makeQuery(id+"F12.imprint","IMPRINT",FACE,{"disambiguationData":[TD([[makeQuery(id+"F12.imprint","IMPRINT",EDGE,{"disambiguationData":[TD([[subQ2,-1.0]])],"derivedFrom":subQ1}),-1.0]])]});}
            var Q2;
            {var subQ0=sQuery(id+"F12.wireOp",EDGE,"E31.2.1");var subQ1=sQuery(id+"F12.wireOp",EDGE,"E31.2.0");var subQ2=makeQuery(id+"F12.imprint","INTERSECT",VERTEX,{"derivedFrom":[subQ1,subQ0]});Q2=makeQuery(id+"F12.imprint","IMPRINT",FACE,{"disambiguationData":[TD([[makeQuery(id+"F12.imprint","IMPRINT",EDGE,{"disambiguationData":[TD([[subQ2,1.0]])],"derivedFrom":subQ1}),-1.0]])]});}
            var Q3;
            {var subQ0=sQuery(id+"F12.wireOp",EDGE,"E31.1.5");var subQ1=sQuery(id+"F12.wireOp",EDGE,"E31.1.4");var subQ2=makeQuery(id+"F12.imprint","INTERSECT",VERTEX,{"derivedFrom":[subQ1,subQ0]});Q3=makeQuery(id+"F12.imprint","IMPRINT",FACE,{"disambiguationData":[TD([[makeQuery(id+"F12.imprint","IMPRINT",EDGE,{"disambiguationData":[TD([[subQ2,-1.0]])],"derivedFrom":subQ1}),-1.0]])]});}
            var Q4;
            {var subQ0=sQuery(id+"F12.wireOp",EDGE,"E31.1.4");var subQ1=sQuery(id+"F12.wireOp",EDGE,"E31.1.0");var subQ2=makeQuery(id+"F12.imprint","INTERSECT",VERTEX,{"derivedFrom":[subQ1,subQ0]});Q4=makeQuery(id+"F12.imprint","IMPRINT",FACE,{"disambiguationData":[TD([[makeQuery(id+"F12.imprint","IMPRINT",EDGE,{"disambiguationData":[TD([[subQ2,-1.0]])],"derivedFrom":subQ1}),-1.0]])]});}
            var Q5;
            {var subQ0=sQuery(id+"F12.wireOp",EDGE,"E31.1.1");var subQ1=sQuery(id+"F12.wireOp",EDGE,"E31.1.0");var subQ2=makeQuery(id+"F12.imprint","INTERSECT",VERTEX,{"derivedFrom":[subQ1,subQ0]});Q5=makeQuery(id+"F12.imprint","IMPRINT",FACE,{"disambiguationData":[TD([[makeQuery(id+"F12.imprint","IMPRINT",EDGE,{"disambiguationData":[TD([[subQ2,1.0]])],"derivedFrom":subQ1}),-1.0]])]});}
            var Q6;
            {var subQ0=sQuery(id+"F12.wireOp",EDGE,"E30.4");var subQ1=sQuery(id+"F6.wireOp",EDGE,"E23.0.3");var subQ2=sQuery(id+"F12.wireOp",EDGE,"E30.3");var subQ3=sQuery(id+"F0.wireOp",EDGE,"E18");var subQ4=sQuery(id+"F0.wireOp",EDGE,"E17");Q6=makeQuery(id+"F13.boolean.opBoolean","MERGE",FACE,{"derivedFrom":[makeQuery(id+"F7.boolean.opBoolean","MERGE",FACE,{"derivedFrom":[makeQuery(id+"F2.opRevolve","SWEPT_FACE",FACE,{"disambiguationData":[OSD([sQuery(id+"F0.wireOp",EDGE,"E16")])]}),makeQuery(id+"F7.opExtrude","CAP_FACE",FACE,{"disambiguationData":[OSD([subQ4,subQ3,sQuery(id+"F6.wireOp",EDGE,"E23.0.1"),sQuery(id+"F6.wireOp",EDGE,"E25")])],"isStart":false}),makeQuery(id+"F7.opExtrude","CAP_FACE",FACE,{"disambiguationData":[OSD([subQ4,subQ3,subQ1,sQuery(id+"F6.wireOp",EDGE,"E24")])],"isStart":false}),makeQuery(id+"F7.opExtrude","CAP_FACE",FACE,{"disambiguationData":[OSD([subQ4,subQ3,sQuery(id+"F6.wireOp",EDGE,"E23.0.5"),sQuery(id+"F6.wireOp",EDGE,"E26")])],"isStart":false})]}),makeQuery(id+"F13.opExtrude","CAP_FACE",FACE,{"disambiguationData":[OSD([subQ1,sQuery(id+"F12.wireOp",EDGE,"E30.2"),subQ2])],"isStart":false}),makeQuery(id+"F13.opExtrude","CAP_FACE",FACE,{"disambiguationData":[OSD([subQ1,subQ2,subQ0])],"isStart":false}),makeQuery(id+"F13.opExtrude","CAP_FACE",FACE,{"disambiguationData":[OSD([subQ1,subQ0,sQuery(id+"F12.wireOp",EDGE,"E30.5")])],"isStart":false})]});}
            extrude(context, id + "F15", {"entities" : qUnion([Q0, Q1, Q2, Q3, Q4, Q5]), "operationType" : NewBodyOperationType.ADD, "endBound" : BoundingType.UP_TO_SURFACE, "oppositeDirection" : true, "endBoundEntityFace" : qUnion([Q6]), "depth" : 25 * mm});
        }
        {
            var Q0;
            Q0=makeQuery(id+"F12.imprint","IMPRINT",FACE,{"disambiguationData":[TD([[makeQuery(id+"F12.imprint","IMPRINT",EDGE,{"derivedFrom":sQuery(id+"F12.wireOp",EDGE,"E31.1.2")}),-1.0]])]});
            var Q1;
            Q1=makeQuery(id+"F12.imprint","IMPRINT",FACE,{"disambiguationData":[TD([[makeQuery(id+"F12.imprint","IMPRINT",EDGE,{"derivedFrom":sQuery(id+"F12.wireOp",EDGE,"E31.2.2")}),-1.0]])]});
            extrude(context, id + "F16", {"entities" : qUnion([Q0, Q1]), "operationType" : NewBodyOperationType.REMOVE, "oppositeDirection" : true, "depth" : 2.5 * mm});
        }
        {
            var Q0;
            {var subQ0=sQuery(id+"F12.wireOp",EDGE,"E31.2.4");var subQ1=sQuery(id+"F6.wireOp",EDGE,"E23.0.1");var subQ2=sQuery(id+"F12.wireOp",EDGE,"E31.2.0");var subQ3=sQuery(id+"F12.wireOp",EDGE,"E31.1.4");var subQ4=sQuery(id+"F6.wireOp",EDGE,"E23.0.5");var subQ5=sQuery(id+"F12.wireOp",EDGE,"E31.1.0");var subQ6=sQuery(id+"F12.wireOp",EDGE,"E30.4");var subQ7=sQuery(id+"F6.wireOp",EDGE,"E23.0.3");var subQ8=sQuery(id+"F12.wireOp",EDGE,"E30.3");var subQ9=sQuery(id+"F0.wireOp",EDGE,"E18");var subQ10=sQuery(id+"F0.wireOp",EDGE,"E17");Q0=makeQuery(id+"F15.boolean.opBoolean","MERGE",FACE,{"derivedFrom":[makeQuery(id+"F13.boolean.opBoolean","MERGE",FACE,{"derivedFrom":[makeQuery(id+"F7.boolean.opBoolean","MERGE",FACE,{"derivedFrom":[makeQuery(id+"F2.opRevolve","SWEPT_FACE",FACE,{"disambiguationData":[OSD([subQ9])]}),makeQuery(id+"F7.opExtrude","CAP_FACE",FACE,{"disambiguationData":[OSD([subQ10,subQ9,subQ1,sQuery(id+"F6.wireOp",EDGE,"E25")])],"isStart":true}),makeQuery(id+"F7.opExtrude","CAP_FACE",FACE,{"disambiguationData":[OSD([subQ10,subQ9,subQ7,sQuery(id+"F6.wireOp",EDGE,"E24")])],"isStart":true}),makeQuery(id+"F7.opExtrude","CAP_FACE",FACE,{"disambiguationData":[OSD([subQ10,subQ9,subQ4,sQuery(id+"F6.wireOp",EDGE,"E26")])],"isStart":true})]}),makeQuery(id+"F13.opExtrude","CAP_FACE",FACE,{"disambiguationData":[OSD([subQ7,sQuery(id+"F12.wireOp",EDGE,"E30.2"),subQ8])],"isStart":true}),makeQuery(id+"F13.opExtrude","CAP_FACE",FACE,{"disambiguationData":[OSD([subQ7,subQ8,subQ6])],"isStart":true}),makeQuery(id+"F13.opExtrude","CAP_FACE",FACE,{"disambiguationData":[OSD([subQ7,subQ6,sQuery(id+"F12.wireOp",EDGE,"E30.5")])],"isStart":true})]}),makeQuery(id+"F15.opExtrude","CAP_FACE",FACE,{"disambiguationData":[OSD([subQ4,subQ5,subQ3])],"isStart":true}),makeQuery(id+"F15.opExtrude","CAP_FACE",FACE,{"disambiguationData":[OSD([subQ4,subQ5,sQuery(id+"F12.wireOp",EDGE,"E31.1.1")])],"isStart":true}),makeQuery(id+"F15.opExtrude","CAP_FACE",FACE,{"disambiguationData":[OSD([subQ4,subQ3,sQuery(id+"F12.wireOp",EDGE,"E31.1.5")])],"isStart":true}),makeQuery(id+"F15.opExtrude","CAP_FACE",FACE,{"disambiguationData":[OSD([subQ1,subQ2,subQ0])],"isStart":true}),makeQuery(id+"F15.opExtrude","CAP_FACE",FACE,{"disambiguationData":[OSD([subQ1,subQ2,sQuery(id+"F12.wireOp",EDGE,"E31.2.1")])],"isStart":true}),makeQuery(id+"F15.opExtrude","CAP_FACE",FACE,{"disambiguationData":[OSD([subQ1,subQ0,sQuery(id+"F12.wireOp",EDGE,"E31.2.5")])],"isStart":true})]});}
            chamfer(context, id + "F17", {"entities" : qUnion([Q0]), "width" : .25 * mm, "tangentPropagation" : true});
        }
        {
            var Q0;
            {var subQ0=sQuery(id+"F0.wireOp",EDGE,"E13");var subQ1=sQuery(id+"F0.wireOp",EDGE,"E12");Q0=makeQuery(id+"F4.boolean.opBoolean","MERGE",FACE,{"derivedFrom":[makeQuery(id+"F2.opRevolve","SWEPT_FACE",FACE,{"disambiguationData":[OSD([sQuery(id+"F0.wireOp",EDGE,"E14")])]}),makeQuery(id+"F4.opExtrude","CAP_FACE",FACE,{"disambiguationData":[OSD([subQ1,subQ0,sQuery(id+"F3.wireOp",EDGE,"E20"),sQuery(id+"F3.wireOp",EDGE,"E21")])],"isStart":false}),makeQuery(id+"F4.opExtrude","CAP_FACE",FACE,{"disambiguationData":[OSD([subQ1,subQ0,sQuery(id+"F3.wireOp",EDGE,"E22.1.0"),sQuery(id+"F3.wireOp",EDGE,"E22.1.1")])],"isStart":false}),makeQuery(id+"F4.opExtrude","CAP_FACE",FACE,{"disambiguationData":[OSD([subQ1,subQ0,sQuery(id+"F3.wireOp",EDGE,"E22.2.0"),sQuery(id+"F3.wireOp",EDGE,"E22.2.1")])],"isStart":false})]});}
            var Q1;
            {var subQ0=sQuery(id+"F12.wireOp",EDGE,"E31.2.4");var subQ1=sQuery(id+"F6.wireOp",EDGE,"E23.0.1");var subQ2=sQuery(id+"F12.wireOp",EDGE,"E31.2.0");var subQ3=sQuery(id+"F12.wireOp",EDGE,"E31.1.4");var subQ4=sQuery(id+"F6.wireOp",EDGE,"E23.0.5");var subQ5=sQuery(id+"F12.wireOp",EDGE,"E31.1.0");var subQ6=sQuery(id+"F12.wireOp",EDGE,"E30.4");var subQ7=sQuery(id+"F6.wireOp",EDGE,"E23.0.3");var subQ8=sQuery(id+"F12.wireOp",EDGE,"E30.3");var subQ9=sQuery(id+"F0.wireOp",EDGE,"E18");var subQ10=sQuery(id+"F0.wireOp",EDGE,"E17");Q1=makeQuery(id+"F15.boolean.opBoolean","MERGE",FACE,{"derivedFrom":[makeQuery(id+"F13.boolean.opBoolean","MERGE",FACE,{"derivedFrom":[makeQuery(id+"F7.boolean.opBoolean","MERGE",FACE,{"derivedFrom":[makeQuery(id+"F2.opRevolve","SWEPT_FACE",FACE,{"disambiguationData":[OSD([sQuery(id+"F0.wireOp",EDGE,"E16")])]}),makeQuery(id+"F7.opExtrude","CAP_FACE",FACE,{"disambiguationData":[OSD([subQ10,subQ9,subQ1,sQuery(id+"F6.wireOp",EDGE,"E25")])],"isStart":false}),makeQuery(id+"F7.opExtrude","CAP_FACE",FACE,{"disambiguationData":[OSD([subQ10,subQ9,subQ7,sQuery(id+"F6.wireOp",EDGE,"E24")])],"isStart":false}),makeQuery(id+"F7.opExtrude","CAP_FACE",FACE,{"disambiguationData":[OSD([subQ10,subQ9,subQ4,sQuery(id+"F6.wireOp",EDGE,"E26")])],"isStart":false})]}),makeQuery(id+"F13.opExtrude","CAP_FACE",FACE,{"disambiguationData":[OSD([subQ7,sQuery(id+"F12.wireOp",EDGE,"E30.2"),subQ8])],"isStart":false}),makeQuery(id+"F13.opExtrude","CAP_FACE",FACE,{"disambiguationData":[OSD([subQ7,subQ8,subQ6])],"isStart":false}),makeQuery(id+"F13.opExtrude","CAP_FACE",FACE,{"disambiguationData":[OSD([subQ7,subQ6,sQuery(id+"F12.wireOp",EDGE,"E30.5")])],"isStart":false})]}),makeQuery(id+"F15.opExtrude","CAP_FACE",FACE,{"disambiguationData":[OSD([subQ4,subQ5,subQ3])],"isStart":false}),makeQuery(id+"F15.opExtrude","CAP_FACE",FACE,{"disambiguationData":[OSD([subQ4,subQ5,sQuery(id+"F12.wireOp",EDGE,"E31.1.1")])],"isStart":false}),makeQuery(id+"F15.opExtrude","CAP_FACE",FACE,{"disambiguationData":[OSD([subQ4,subQ3,sQuery(id+"F12.wireOp",EDGE,"E31.1.5")])],"isStart":false}),makeQuery(id+"F15.opExtrude","CAP_FACE",FACE,{"disambiguationData":[OSD([subQ1,subQ2,subQ0])],"isStart":false}),makeQuery(id+"F15.opExtrude","CAP_FACE",FACE,{"disambiguationData":[OSD([subQ1,subQ2,sQuery(id+"F12.wireOp",EDGE,"E31.2.1")])],"isStart":false}),makeQuery(id+"F15.opExtrude","CAP_FACE",FACE,{"disambiguationData":[OSD([subQ1,subQ0,sQuery(id+"F12.wireOp",EDGE,"E31.2.5")])],"isStart":false})]});}
            var Q2;
            {var subQ0=sQuery(id+"F0.wireOp",EDGE,"E13");var subQ1=sQuery(id+"F0.wireOp",EDGE,"E12");Q2=makeQuery(id+"F4.boolean.opBoolean","MERGE",FACE,{"derivedFrom":[makeQuery(id+"F2.opRevolve","SWEPT_FACE",FACE,{"disambiguationData":[OSD([subQ1])]}),makeQuery(id+"F4.opExtrude","CAP_FACE",FACE,{"disambiguationData":[OSD([subQ1,subQ0,sQuery(id+"F3.wireOp",EDGE,"E20"),sQuery(id+"F3.wireOp",EDGE,"E21")])],"isStart":true}),makeQuery(id+"F4.opExtrude","CAP_FACE",FACE,{"disambiguationData":[OSD([subQ1,subQ0,sQuery(id+"F3.wireOp",EDGE,"E22.1.0"),sQuery(id+"F3.wireOp",EDGE,"E22.1.1")])],"isStart":true}),makeQuery(id+"F4.opExtrude","CAP_FACE",FACE,{"disambiguationData":[OSD([subQ1,subQ0,sQuery(id+"F3.wireOp",EDGE,"E22.2.0"),sQuery(id+"F3.wireOp",EDGE,"E22.2.1")])],"isStart":true})]});}
            chamfer(context, id + "F18", {"entities" : qUnion([Q0, Q1, Q2]), "width" : .5 * mm, "tangentPropagation" : true});
        }
    });
